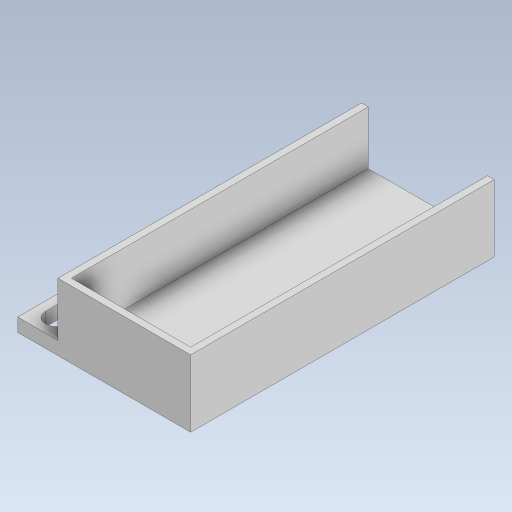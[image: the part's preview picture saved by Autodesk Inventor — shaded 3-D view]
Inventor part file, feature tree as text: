
AUTODESK INVENTOR PART (.ipt)
format: ipt  version: 2023.5 (Build 275446000, 446)  size: 127,488 bytes
history: native  units: mm
features: extrude x2, sketch x1
ambient origin geometry x8: Origin, YZ Plane, XZ Plane, XY Plane, X Axis, Y Axis, Z Axis, Center Point
bodies: Solid1 (feature_tree)
feature tree (3):
  sketch  "Sketch1"  dims[d0=17.8mm d1=43.3mm d2=19.8mm d3=45.3mm d4=6.0mm d5=3.3mm d6=40.0mm d7=2.5mm d8=2.0mm d9=0.0mm d10=10.0mm d11=0.0mm]
  extrude  "Extrusion1"  Depth=10.0mm
  extrude  "Extrusion2"  Depth=19.8mm
